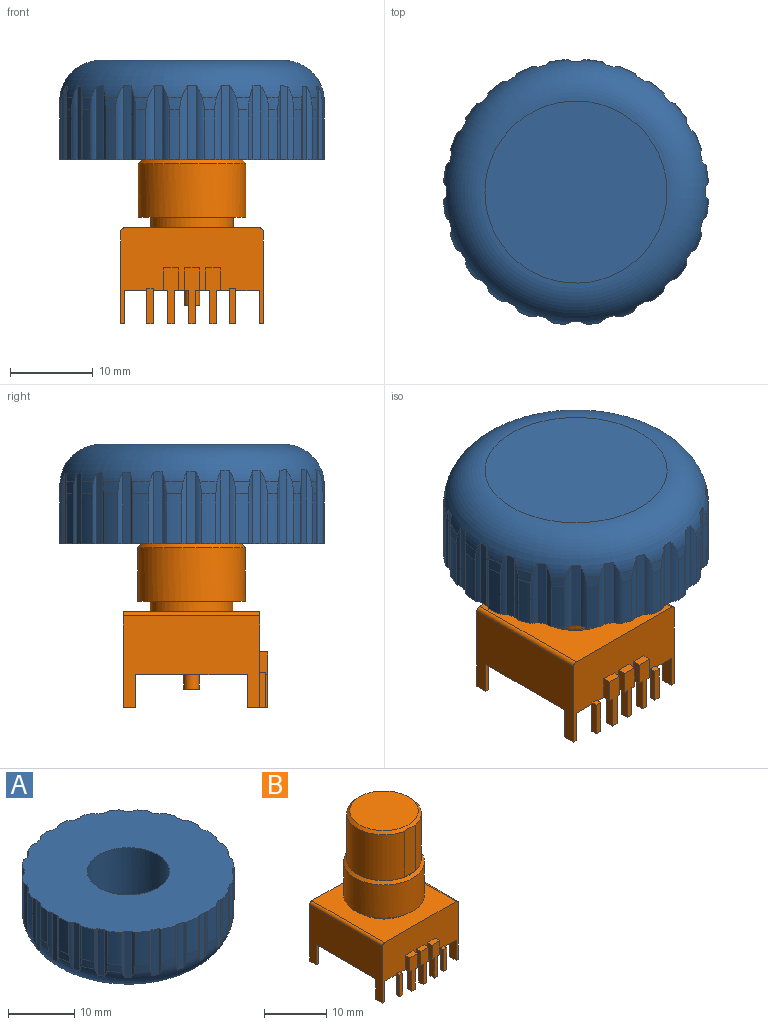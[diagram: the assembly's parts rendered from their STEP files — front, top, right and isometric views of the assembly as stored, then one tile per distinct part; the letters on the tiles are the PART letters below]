
ASSEMBLY  parts=2 mates=1
PART A: 125 faces, bbox 34.6x34.6x12 mm
  f0: sphere r=16.05mm, area 2.5mm2, adj f40,f75,f79,f124
  f1: sphere r=16.05mm, area 2.7mm2, adj f41,f72,f76,f124
  f2: sphere r=16.05mm, area 2.8mm2, adj f42,f69,f73,f124
  f3: sphere r=16.05mm, area 3mm2, adj f43,f66,f70,f124
  f4: sphere r=16.05mm, area 3.1mm2, adj f44,f63,f67,f124
  f5: sphere r=16.05mm, area 3.3mm2, adj f45,f60,f64,f124
  f6: sphere r=16.05mm, area 3.4mm2, adj f46,f57,f61,f124
  f7: sphere r=16.05mm, area 3.4mm2, adj f47,f54,f58,f124
  f8: sphere r=16.05mm, area 3.5mm2, adj f48,f51,f55,f124
  f9: sphere r=16.05mm, area 3.5mm2, adj f49,f52,f120,f124
  f10: sphere r=16.05mm, area 3.4mm2, adj f26,f117,f121,f124
  f11: sphere r=16.05mm, area 3.4mm2, adj f27,f114,f118,f124
  f12: sphere r=16.05mm, area 3.3mm2, adj f28,f111,f115,f124
  f13: sphere r=16.05mm, area 3.1mm2, adj f29,f108,f112,f124
  f14: sphere r=16.05mm, area 3mm2, adj f30,f105,f109,f124
  f15: sphere r=16.05mm, area 2.8mm2, adj f31,f102,f106,f124
  f16: sphere r=16.05mm, area 2.7mm2, adj f32,f99,f103,f124
  f17: sphere r=16.05mm, area 2.5mm2, adj f33,f96,f100,f124
  f18: sphere r=16.05mm, area 2.3mm2, adj f34,f93,f97,f124
  f19: sphere r=16.05mm, area 2.2mm2, adj f35,f90,f94,f124
  f20: sphere r=16.05mm, area 2.2mm2, adj f36,f87,f91,f124
  f21: sphere r=16.05mm, area 2.2mm2, adj f37,f84,f88,f124
  f22: sphere r=16.05mm, area 2.2mm2, adj f38,f81,f85,f124
  f23: cylinder r=6.2mm len=12.4mm, axis (0,0,-1), area 389.6mm2, adj f24,f25
  f24: plane 12.4x12.4mm, normal (0,0,1), area 120.8mm2, adj f23
  f25: plane 32.02x32mm, normal (0,0,1), area 674.4mm2, adj f23,f26,f27,f28,f29,f30,f31,f32
  f26: cylinder r=16.05mm len=6mm, axis (0,0,1), area 13.4mm2, adj f10,f25,f117,f121
  f27: cylinder r=16.05mm len=6mm, axis (0,0,1), area 13.1mm2, adj f11,f25,f114,f118
  f28: cylinder r=16.05mm len=6mm, axis (0,0,1), area 12.7mm2, adj f12,f25,f111,f115
  f29: cylinder r=16.05mm len=6mm, axis (0,0,1), area 12.1mm2, adj f13,f25,f108,f112
  f30: cylinder r=16.05mm len=6mm, axis (0,0,1), area 11.5mm2, adj f14,f25,f105,f109
  f31: cylinder r=16.05mm len=6mm, axis (0,0,1), area 10.7mm2, adj f15,f25,f102,f106
  f32: cylinder r=16.05mm len=6mm, axis (0,0,1), area 9.9mm2, adj f16,f25,f99,f103
  f33: cylinder r=16.05mm len=6mm, axis (0,0,1), area 9.2mm2, adj f17,f25,f96,f100
  f34: cylinder r=16.05mm len=6mm, axis (0,0,1), area 8.4mm2, adj f18,f25,f93,f97
  f35: cylinder r=16.05mm len=6mm, axis (0,0,1), area 7.9mm2, adj f19,f25,f90,f94
  f36: cylinder r=16.05mm len=6mm, axis (0,0,1), area 7.5mm2, adj f20,f25,f87,f91
  f37: cylinder r=16.05mm len=6mm, axis (0,0,1), area 7.5mm2, adj f21,f25,f84,f88
  f38: cylinder r=16.05mm len=6mm, axis (0,0,1), area 7.9mm2, adj f22,f25,f81,f85
  f39: cylinder r=16.05mm len=6mm, axis (0,0,1), area 8.4mm2, adj f25,f50,f78,f82
  f40: cylinder r=16.05mm len=6mm, axis (0,0,1), area 9.2mm2, adj f0,f25,f75,f79
  f41: cylinder r=16.05mm len=6mm, axis (0,0,1), area 9.9mm2, adj f1,f25,f72,f76
  f42: cylinder r=16.05mm len=6mm, axis (0,0,1), area 10.7mm2, adj f2,f25,f69,f73
  f43: cylinder r=16.05mm len=6mm, axis (0,0,1), area 11.5mm2, adj f3,f25,f66,f70
  f44: cylinder r=16.05mm len=6mm, axis (0,0,1), area 12.1mm2, adj f4,f25,f63,f67
  f45: cylinder r=16.05mm len=6mm, axis (0,0,1), area 12.7mm2, adj f5,f25,f60,f64
  f46: cylinder r=16.05mm len=6mm, axis (0,0,1), area 13.1mm2, adj f6,f25,f57,f61
  f47: cylinder r=16.05mm len=6mm, axis (0,0,1), area 13.4mm2, adj f7,f25,f54,f58
  f48: cylinder r=16.05mm len=6mm, axis (0,0,1), area 13.5mm2, adj f8,f25,f51,f55
  f49: cylinder r=16.05mm len=6mm, axis (0,0,1), area 13.5mm2, adj f9,f25,f52,f120
  f50: sphere r=16.05mm, area 2.3mm2, adj f39,f78,f82,f124
  f51: cylinder r=2mm len=8.44mm, axis (0,0,1), area 3.6mm2, adj f8,f25,f48,f53,f124
  f52: cylinder r=2mm len=8.44mm, axis (0,0,1), area 3.6mm2, adj f9,f25,f49,f53,f124
  f53: cylinder r=15.7mm len=8.44mm, axis (0,0,-1), area 9.2mm2, adj f25,f51,f52,f124
  f54: cylinder r=2mm len=8.45mm, axis (0,0,1), area 3.7mm2, adj f7,f25,f47,f56,f124
  f55: cylinder r=2mm len=8.45mm, axis (0,0,1), area 3.6mm2, adj f8,f25,f48,f56,f124
  f56: cylinder r=15.7mm len=8.45mm, axis (0,0,-1), area 9.3mm2, adj f25,f54,f55,f124
  f57: cylinder r=2mm len=8.49mm, axis (0,0,1), area 3.9mm2, adj f6,f25,f46,f59,f124
  f58: cylinder r=2mm len=8.47mm, axis (0,0,1), area 3.8mm2, adj f7,f25,f47,f59,f124
  f59: cylinder r=15.7mm len=8.49mm, axis (0,0,-1), area 9.3mm2, adj f25,f57,f58,f124
  f60: cylinder r=2mm len=8.53mm, axis (0,0,1), area 4.2mm2, adj f5,f25,f45,f62,f124
  f61: cylinder r=2mm len=8.52mm, axis (0,0,1), area 4mm2, adj f6,f25,f46,f62,f124
  f62: cylinder r=15.7mm len=8.53mm, axis (0,0,-1), area 9.3mm2, adj f25,f60,f61,f124
  f63: cylinder r=2mm len=8.59mm, axis (0,0,1), area 4.6mm2, adj f4,f25,f44,f65,f124
  f64: cylinder r=2mm len=8.58mm, axis (0,0,1), area 4.4mm2, adj f5,f25,f45,f65,f124
  f65: cylinder r=15.7mm len=8.59mm, axis (0,0,-1), area 9.4mm2, adj f25,f63,f64,f124
  f66: cylinder r=2mm len=8.66mm, axis (0,0,1), area 5.1mm2, adj f3,f25,f43,f68,f124
  f67: cylinder r=2mm len=8.64mm, axis (0,0,1), area 4.8mm2, adj f4,f25,f44,f68,f124
  f68: cylinder r=15.7mm len=8.66mm, axis (0,0,-1), area 9.5mm2, adj f25,f66,f67,f124
  f69: cylinder r=2mm len=8.73mm, axis (0,0,1), area 5.6mm2, adj f2,f25,f42,f71,f124
  f70: cylinder r=2mm len=8.71mm, axis (0,0,1), area 5.3mm2, adj f3,f25,f43,f71,f124
  f71: cylinder r=15.7mm len=8.73mm, axis (0,0,-1), area 9.6mm2, adj f25,f69,f70,f124
  f72: cylinder r=2mm len=8.79mm, axis (0,0,1), area 6.2mm2, adj f1,f25,f41,f74,f124
  f73: cylinder r=2mm len=8.77mm, axis (0,0,1), area 5.9mm2, adj f2,f25,f42,f74,f124
  f74: cylinder r=15.7mm len=8.79mm, axis (0,0,-1), area 9.6mm2, adj f25,f72,f73,f124
  f75: cylinder r=2mm len=8.85mm, axis (0,0,1), area 6.8mm2, adj f0,f25,f40,f77,f124
  f76: cylinder r=2mm len=8.83mm, axis (0,0,1), area 6.4mm2, adj f1,f25,f41,f77,f124
  f77: cylinder r=15.7mm len=8.85mm, axis (0,0,-1), area 9.7mm2, adj f25,f75,f76,f124
  f78: cylinder r=2mm len=8.89mm, axis (0,0,1), area 7.3mm2, adj f25,f39,f50,f80,f124
  f79: cylinder r=2mm len=8.88mm, axis (0,0,1), area 7mm2, adj f0,f25,f40,f80,f124
  f80: cylinder r=15.7mm len=8.89mm, axis (0,0,-1), area 9.7mm2, adj f25,f78,f79,f124
  f81: cylinder r=2mm len=8.93mm, axis (0,0,1), area 7.8mm2, adj f22,f25,f38,f83,f124
  f82: cylinder r=2mm len=8.92mm, axis (0,0,1), area 7.5mm2, adj f25,f39,f50,f83,f124
  f83: cylinder r=15.7mm len=8.93mm, axis (0,0,-1), area 9.8mm2, adj f25,f81,f82,f124
  f84: cylinder r=2mm len=8.95mm, axis (0,0,1), area 8mm2, adj f21,f25,f37,f86,f124
  f85: cylinder r=2mm len=8.94mm, axis (0,0,1), area 7.9mm2, adj f22,f25,f38,f86,f124
  f86: cylinder r=15.7mm len=8.95mm, axis (0,0,-1), area 9.8mm2, adj f25,f84,f85,f124
  f87: cylinder r=2mm len=8.95mm, axis (0,0,1), area 8mm2, adj f20,f25,f36,f89,f124
  f88: cylinder r=2mm len=8.95mm, axis (0,0,1), area 8mm2, adj f21,f25,f37,f89,f124
  f89: cylinder r=15.7mm len=8.95mm, axis (0,0,-1), area 9.8mm2, adj f25,f87,f88,f124
  f90: cylinder r=2mm len=8.94mm, axis (0,0,1), area 7.9mm2, adj f19,f25,f35,f92,f124
  f91: cylinder r=2mm len=8.95mm, axis (0,0,1), area 8mm2, adj f20,f25,f36,f92,f124
  f92: cylinder r=15.7mm len=8.95mm, axis (0,0,-1), area 9.8mm2, adj f25,f90,f91,f124
  f93: cylinder r=2mm len=8.92mm, axis (0,0,1), area 7.5mm2, adj f18,f25,f34,f95,f124
  f94: cylinder r=2mm len=8.93mm, axis (0,0,1), area 7.8mm2, adj f19,f25,f35,f95,f124
  f95: cylinder r=15.7mm len=8.93mm, axis (0,0,-1), area 9.8mm2, adj f25,f93,f94,f124
  f96: cylinder r=2mm len=8.88mm, axis (0,0,1), area 7mm2, adj f17,f25,f33,f98,f124
  f97: cylinder r=2mm len=8.89mm, axis (0,0,1), area 7.3mm2, adj f18,f25,f34,f98,f124
  f98: cylinder r=15.7mm len=8.89mm, axis (0,0,-1), area 9.7mm2, adj f25,f96,f97,f124
  f99: cylinder r=2mm len=8.83mm, axis (0,0,1), area 6.4mm2, adj f16,f25,f32,f101,f124
  f100: cylinder r=2mm len=8.85mm, axis (0,0,1), area 6.8mm2, adj f17,f25,f33,f101,f124
  f101: cylinder r=15.7mm len=8.85mm, axis (0,0,-1), area 9.7mm2, adj f25,f99,f100,f124
  f102: cylinder r=2mm len=8.77mm, axis (0,0,1), area 5.9mm2, adj f15,f25,f31,f104,f124
  f103: cylinder r=2mm len=8.79mm, axis (0,0,1), area 6.2mm2, adj f16,f25,f32,f104,f124
  f104: cylinder r=15.7mm len=8.79mm, axis (0,0,-1), area 9.6mm2, adj f25,f102,f103,f124
  f105: cylinder r=2mm len=8.71mm, axis (0,0,1), area 5.3mm2, adj f14,f25,f30,f107,f124
  f106: cylinder r=2mm len=8.73mm, axis (0,0,1), area 5.6mm2, adj f15,f25,f31,f107,f124
  f107: cylinder r=15.7mm len=8.73mm, axis (0,0,-1), area 9.6mm2, adj f25,f105,f106,f124
  f108: cylinder r=2mm len=8.64mm, axis (0,0,1), area 4.8mm2, adj f13,f25,f29,f110,f124
  f109: cylinder r=2mm len=8.66mm, axis (0,0,1), area 5.1mm2, adj f14,f25,f30,f110,f124
  f110: cylinder r=15.7mm len=8.66mm, axis (0,0,-1), area 9.5mm2, adj f25,f108,f109,f124
  f111: cylinder r=2mm len=8.58mm, axis (0,0,1), area 4.4mm2, adj f12,f25,f28,f113,f124
  f112: cylinder r=2mm len=8.59mm, axis (0,0,1), area 4.6mm2, adj f13,f25,f29,f113,f124
  f113: cylinder r=15.7mm len=8.59mm, axis (0,0,-1), area 9.4mm2, adj f25,f111,f112,f124
  f114: cylinder r=2mm len=8.52mm, axis (0,0,1), area 4mm2, adj f11,f25,f27,f116,f124
  f115: cylinder r=2mm len=8.53mm, axis (0,0,1), area 4.2mm2, adj f12,f25,f28,f116,f124
  f116: cylinder r=15.7mm len=8.53mm, axis (0,0,-1), area 9.3mm2, adj f25,f114,f115,f124
  f117: cylinder r=2mm len=8.47mm, axis (0,0,1), area 3.8mm2, adj f10,f25,f26,f119,f124
  f118: cylinder r=2mm len=8.49mm, axis (0,0,1), area 3.9mm2, adj f11,f25,f27,f119,f124
  f119: cylinder r=15.7mm len=8.49mm, axis (0,0,-1), area 9.3mm2, adj f25,f117,f118,f124
  f120: cylinder r=2mm len=8.45mm, axis (0,0,1), area 3.6mm2, adj f9,f25,f49,f122,f124
  f121: cylinder r=2mm len=8.45mm, axis (0,0,1), area 3.7mm2, adj f10,f25,f26,f122,f124
  f122: cylinder r=15.7mm len=8.45mm, axis (0,0,-1), area 9.3mm2, adj f25,f120,f121,f124
  f123: plane 22.01x22.01mm, normal (0,0,-1), area 380.5mm2, adj f124
  f124: torus R=11mm, axis (0,0,-1), area 605.1mm2, adj f0,f1,f2,f3,f4,f5,f6,f7
PART B: 70 faces, bbox 17.3x17.5x29.4 mm
  f0: cylinder r=6mm len=11.75mm, axis (0,0,-1), area 147.6mm2, adj f1,f7,f8,f10
  f1: cone r=5.5mm half-angle=45deg, axis (0,0,-1), area 25mm2, adj f0,f5,f6,f8,f10
  f2: cylinder r=5mm len=10mm, axis (0,0,-1), area 39.3mm2, adj f4,f16
  f3: cylinder r=6.5mm len=13mm, axis (0,0,-1), area 265.5mm2, adj f4,f7
  f4: plane 13x13mm, normal (0,0,-1), area 54.2mm2, adj f2,f3
  f5: cylinder r=6mm len=11.75mm, axis (0,0,-1), area 147.6mm2, adj f1,f7,f8,f10
  f6: plane 11x11mm, normal (0,0,1), area 95mm2, adj f1
  f7: cone r=6mm half-angle=45deg, axis (0,0,-1), area 27.8mm2, adj f0,f3,f5,f9,f11
  f8: plane 9.13x2.44mm, normal (0,1,0), area 22.1mm2, adj f0,f1,f5,f9
  f9: plane 2.44x0.13mm, normal (0,0,1), area 0.2mm2, adj f7,f8
  f10: plane 9.13x2.44mm, normal (0,-1,0), area 22.1mm2, adj f0,f1,f5,f11
  f11: plane 2.44x0.13mm, normal (0,0,1), area 0.2mm2, adj f7,f10
  f12: plane 17.25x11.6mm, normal (0,-1,0), area 120.2mm2, adj f13,f15,f16,f17,f20,f22,f23,f25
  f13: plane 16.5x11.1mm, normal (1,0,0), area 129.1mm2, adj f12,f14,f17,f24,f25,f30,f31,f32
  f14: plane 17.25x11.6mm, normal (0,1,0), area 135mm2, adj f13,f15,f16,f17,f26,f28,f29,f31
  f15: plane 16.5x11.1mm, normal (-1,0,0), area 129.1mm2, adj f12,f14,f17,f21,f22,f27,f28,f33
  f16: plane 16.5x16.25mm, normal (0,0,1), area 189.6mm2, adj f2,f12,f14,f32,f33
  f17: plane 17.5x17.25mm, normal (0,0,-1), area 281.9mm2, adj f12,f13,f14,f15,f18,f20,f21,f23
  f18: cylinder r=0.93mm len=1.85mm, axis (0,0,1), area 10.2mm2, adj f17,f19
  f19: plane 1.85x1.85mm, normal (0,0,-1), area 2.7mm2, adj f18
  f20: plane 4x1.5mm, normal (1,0,0), area 6mm2, adj f12,f17,f21,f22
  f21: plane 4x0.5mm, normal (0,1,0), area 2mm2, adj f15,f17,f20,f22
  f22: plane 1.5x0.5mm, normal (0,0,-1), area 0.8mm2, adj f12,f15,f20,f21
  f23: plane 4x1.5mm, normal (-1,0,0), area 6mm2, adj f12,f17,f24,f25
  f24: plane 4x0.5mm, normal (0,1,0), area 2mm2, adj f13,f17,f23,f25
  f25: plane 1.5x0.5mm, normal (0,0,-1), area 0.8mm2, adj f12,f13,f23,f24
  f26: plane 4x1.5mm, normal (1,0,0), area 6mm2, adj f14,f17,f27,f28
  f27: plane 4x0.5mm, normal (0,-1,0), area 2mm2, adj f15,f17,f26,f28
  f28: plane 1.5x0.5mm, normal (0,0,-1), area 0.8mm2, adj f14,f15,f26,f27
  f29: plane 4x1.5mm, normal (-1,0,0), area 6mm2, adj f14,f17,f30,f31
  f30: plane 4x0.5mm, normal (0,-1,0), area 2mm2, adj f13,f17,f29,f31
  f31: plane 1.5x0.5mm, normal (0,0,-1), area 0.8mm2, adj f13,f14,f29,f30
  f32: cylinder r=0.5mm len=16.5mm, axis (0,-1,0), area 13mm2, adj f12,f13,f14,f16
  f33: cylinder r=0.5mm len=16.5mm, axis (0,1,0), area 13mm2, adj f12,f14,f15,f16
  f34: plane 2.75x1mm, normal (1,0,0), area 2.7mm2, adj f12,f17,f35,f40
  f35: plane 1.75x1mm, normal (0,0,1), area 1.7mm2, adj f12,f34,f36,f40
  f36: plane 2.75x1mm, normal (-1,0,0), area 2.7mm2, adj f12,f17,f35,f40
  f37: plane 4x1mm, normal (-1,0,0), area 4mm2, adj f17,f38,f40,f41
  f38: plane 1x0.75mm, normal (0,0,-1), area 0.7mm2, adj f37,f39,f40,f41
  f39: plane 4x1mm, normal (1,0,0), area 4mm2, adj f17,f38,f40,f41
  f40: plane 6.75x1.75mm, normal (0,-1,0), area 7.8mm2, adj f17,f34,f35,f36,f37,f38,f39
  f41: plane 4x0.75mm, normal (0,1,0), area 3mm2, adj f17,f37,f38,f39
  f42: plane 4x0.75mm, normal (0,1,0), area 3mm2, adj f17,f46,f47,f48
  f43: plane 2.75x1mm, normal (1,0,0), area 2.7mm2, adj f12,f17,f44,f49
  f44: plane 1.75x1mm, normal (0,0,1), area 1.7mm2, adj f12,f43,f45,f49
  f45: plane 2.75x1mm, normal (-1,0,0), area 2.7mm2, adj f12,f17,f44,f49
  f46: plane 4x1mm, normal (-1,0,0), area 4mm2, adj f17,f42,f47,f49
  f47: plane 1x0.75mm, normal (0,0,-1), area 0.7mm2, adj f42,f46,f48,f49
  f48: plane 4x1mm, normal (1,0,0), area 4mm2, adj f17,f42,f47,f49
  f49: plane 6.75x1.75mm, normal (0,-1,0), area 7.8mm2, adj f17,f43,f44,f45,f46,f47,f48
  f50: plane 4x0.75mm, normal (0,1,0), area 3mm2, adj f17,f54,f55,f56
  f51: plane 2.75x1mm, normal (1,0,0), area 2.7mm2, adj f12,f17,f52,f57
  f52: plane 1.75x1mm, normal (0,0,1), area 1.7mm2, adj f12,f51,f53,f57
  f53: plane 2.75x1mm, normal (-1,0,0), area 2.7mm2, adj f12,f17,f52,f57
  f54: plane 4x1mm, normal (-1,0,0), area 4mm2, adj f17,f50,f55,f57
  f55: plane 1x0.75mm, normal (0,0,-1), area 0.7mm2, adj f50,f54,f56,f57
  f56: plane 4x1mm, normal (1,0,0), area 4mm2, adj f17,f50,f55,f57
  f57: plane 6.75x1.75mm, normal (0,-1,0), area 7.8mm2, adj f17,f51,f52,f53,f54,f55,f56
  f58: plane 4.25x0.75mm, normal (-1,0,0), area 3.2mm2, adj f12,f59,f61,f62,f63
  f59: plane 0.75x0.75mm, normal (0,0,-1), area 0.6mm2, adj f58,f60,f62,f63
  f60: plane 4.25x0.75mm, normal (1,0,0), area 3.2mm2, adj f12,f59,f61,f62,f63
  f61: plane 0.75x0.75mm, normal (0,0,1), area 0.6mm2, adj f12,f58,f60,f62
  f62: plane 4.25x0.75mm, normal (0,-1,0), area 3.2mm2, adj f58,f59,f60,f61
  f63: plane 4x0.75mm, normal (0,1,0), area 3mm2, adj f17,f58,f59,f60
  f64: plane 4.25x0.75mm, normal (-1,0,0), area 3.2mm2, adj f12,f65,f67,f68,f69
  f65: plane 0.75x0.75mm, normal (0,0,-1), area 0.6mm2, adj f64,f66,f68,f69
  f66: plane 4.25x0.75mm, normal (1,0,0), area 3.2mm2, adj f12,f65,f67,f68,f69
  f67: plane 0.75x0.75mm, normal (0,0,1), area 0.6mm2, adj f12,f64,f66,f68
  f68: plane 4.25x0.75mm, normal (0,-1,0), area 3.2mm2, adj f64,f65,f66,f67
  f69: plane 4x0.75mm, normal (0,1,0), area 3mm2, adj f17,f64,f65,f66
PLACE A rot(axis=(1,0,0),180deg) t=(0,0,0.5)mm
PLACE B t=(0,0.09,4)mm
MATE fastened A.f23 <-> B.f0  axis (0,0,-1) through (0,0.09,29.85)mm
